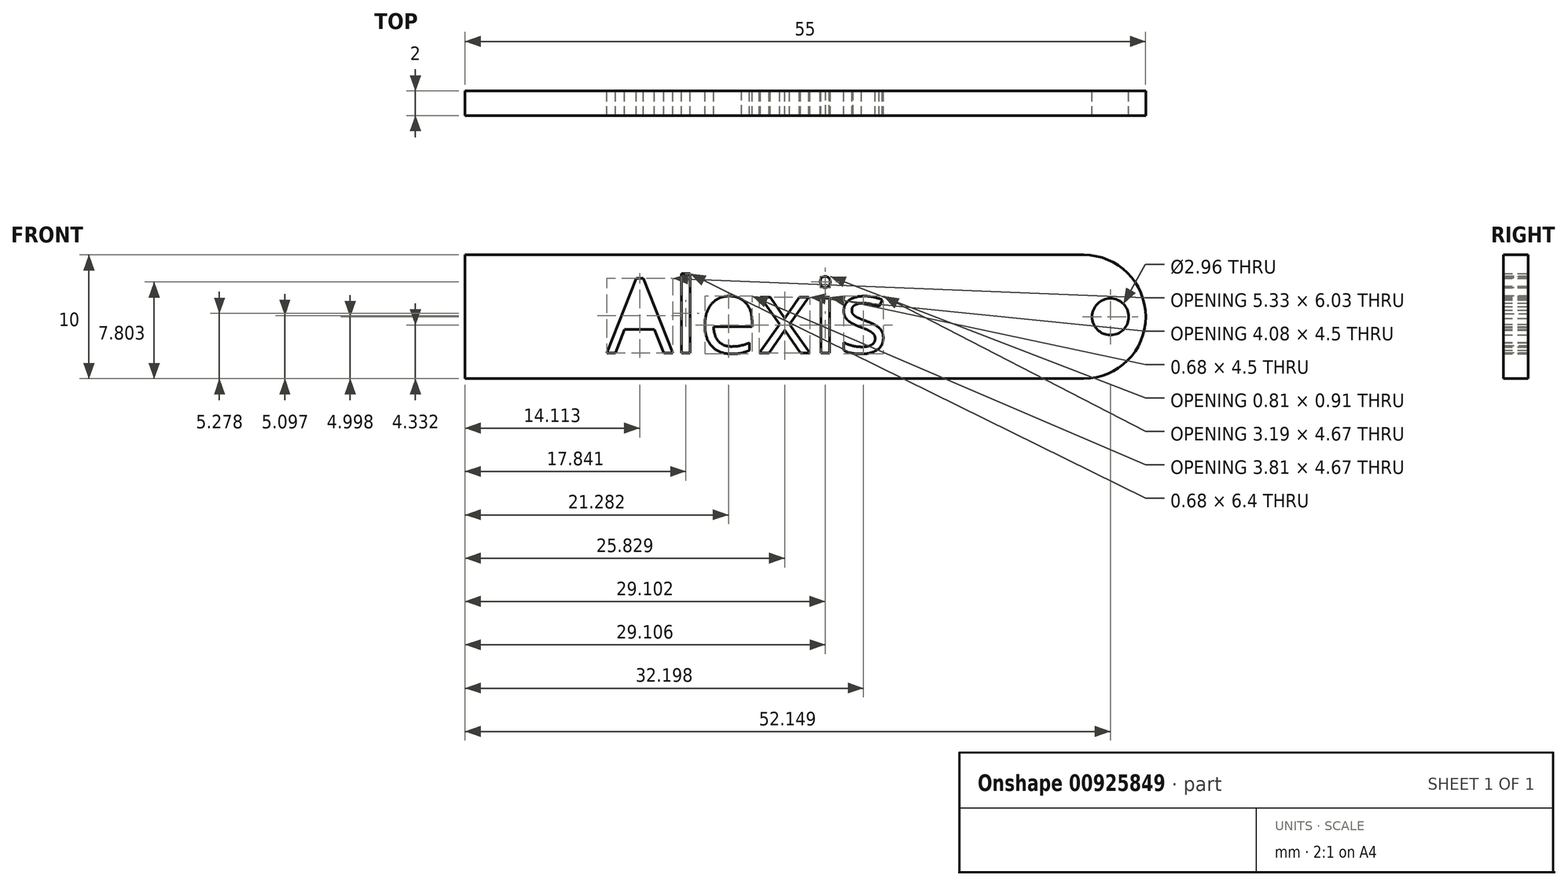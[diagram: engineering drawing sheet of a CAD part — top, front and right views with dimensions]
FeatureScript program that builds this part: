
annotation { "Feature Type Name" : "Feature", "Feature Type Description" : "" }
export const myFeature = defineFeature(function(context is Context, id is Id, definition is map)
    precondition{}
    {
        {
            var Q0;
            Q0=qCreatedBy(makeId("Front.planeOp"),FACE);
            var sketch = newSketch(context, id + "F0", { "sketchPlane" : qUnion([Q0])});
            skLineSegment(sketch, "E0.bottom", {"start": v(-34.35, 28.57) * mm, "end": v(15.65, 28.57) * mm});
            skLineSegment(sketch, "E0.top", {"start": v(-34.35, 18.57) * mm, "end": v(15.65, 18.57) * mm});
            skLineSegment(sketch, "E0.left", {"start": v(-34.35, 28.57) * mm, "end": v(-34.35, 18.57) * mm});
            skArc(sketch, "E1", {"start": v(15.65, 18.57) * mm, "mid": v(20.65, 23.57) * mm, "end": v(15.65, 28.57) * mm});
            skCircle(sketch, "E2", {"center": v(17.8, 23.57) * mm, "radius": 1.48 * mm});
            skText(sketch, "E3", { "text": "Alexis", "fontName": "OpenSans-Regular.ttf"});
            const initialGuessF0  = {"E3": [-0.0229, 0.02065, 1, 0, 0.00606]};
            skSetInitialGuess(sketch, initialGuessF0);
            skSolve(sketch);
        }
        {
            var Q0;
            Q0=makeQuery(id+"F0.imprint","IMPRINT",FACE,{"disambiguationData":[TD([[makeQuery(id+"F0.imprint","IMPRINT",EDGE,{"derivedFrom":sQuery(id+"F0.wireOp",EDGE,"E0.bottom")}),-1.0]])]});
            extrude(context, id + "F1", {"entities" : qUnion([Q0]), "depth" : 2 * mm, "offsetDistance" : 25 * mm});
        }
    });
